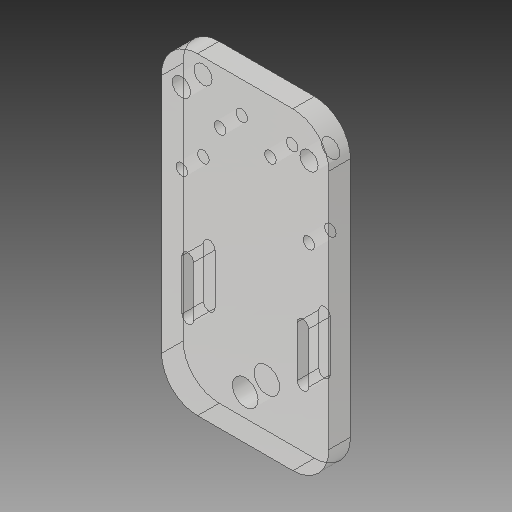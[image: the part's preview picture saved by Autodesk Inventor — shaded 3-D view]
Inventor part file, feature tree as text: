
AUTODESK INVENTOR PART (.ipt)
format: ipt  version: 2018 (Build 220112000, 112)  size: 209,920 bytes
history: native  units: in
note: dims shown in document units (in); Inventor stores cm internally (conversion verified against a paired STEP export)
features: reference x10, other x5, sketch x2, extrude x1
ambient origin geometry x8: Origin, YZ Plane, XZ Plane, XY Plane, X Axis, Y Axis, Z Axis, Center Point
bodies: Solid1 (feature_tree)
feature tree (18):
  sketch  "Sketch1"  dims[d7=0.2362in d8=0.0in]
  extrude  "Extrusion1"  [1 undecoded]
  reference  "Reference1"
  reference  "Reference2"
  reference  "Reference3"
  reference  "Reference4"
  sketch  "Sketch2"
  reference  "Reference5"
  reference  "Reference6"
  reference  "Reference7"
  reference  "Reference8"
  reference  "Reference9"
  reference  "Reference10"
  other  "<userpath>\OneDrive\Inventor\Beast 3D Printer\Hotend Mount Assembly.iam"
  other  "Hotend Mount Assembly.iam"
  other  "Hotend Front Plate:1"
  other  "Hotend Slide Part3:1"
  other  "Hotend Slide Part 1:1"
note: 1 required parameter value undecoded (feature->parameter linkage not recoverable at this tier; creation-order binding heuristic only, values carry confidence <= 0.55)
